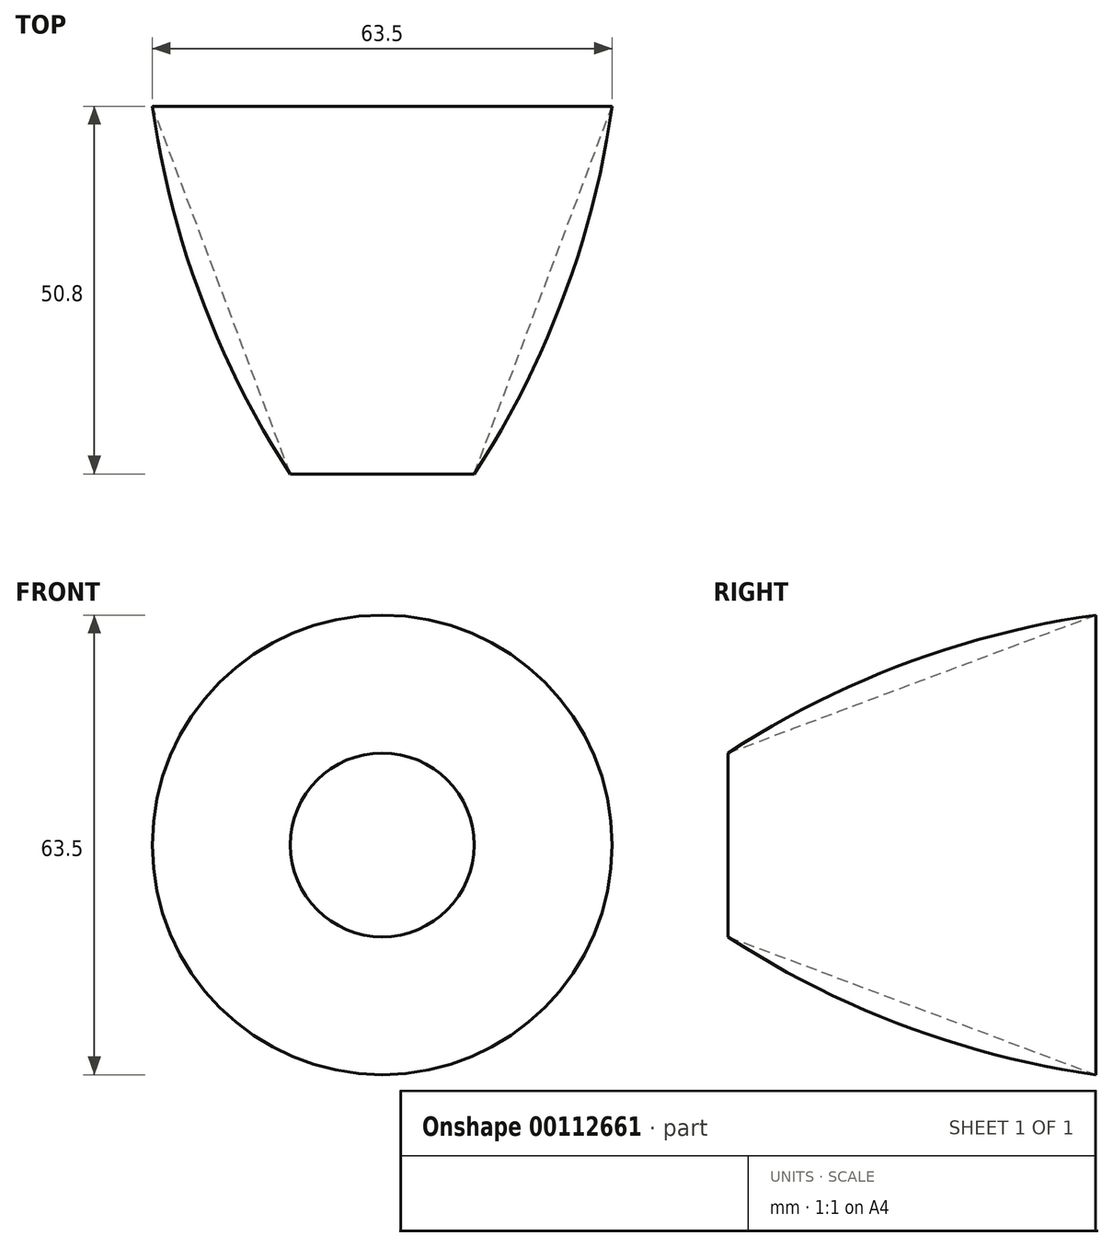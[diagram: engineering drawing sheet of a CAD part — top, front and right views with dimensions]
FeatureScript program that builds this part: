
annotation { "Feature Type Name" : "Feature", "Feature Type Description" : "" }
export const myFeature = defineFeature(function(context is Context, id is Id, definition is map)
    precondition{}
    {
        {
            var Q0;
            Q0=qCreatedBy(makeId("Top.planeOp"),FACE);
            var sketch = newSketch(context, id + "F0", { "sketchPlane" : qUnion([Q0])});
            skLineSegment(sketch, "E0", {"start": v(0, 0) * mm, "end": v(12.7, 0) * mm});
            skLineSegment(sketch, "E1", {"start": v(12.7, 0) * mm, "end": v(12.7, 50.8) * mm, "construction": true});
            skLineSegment(sketch, "E2", {"start": v(12.7, 50.8) * mm, "end": v(31.75, 50.8) * mm, "construction": true});
            skArc(sketch, "E3", {"start": v(12.7, 0) * mm, "mid": v(25.01, 24.35) * mm, "end": v(31.75, 50.8) * mm});
            skLineSegment(sketch, "E4", {"start": v(12.7, 0) * mm, "end": v(31.75, 50.8) * mm});
            skLineSegment(sketch, "E5", {"start": v(12.7, 25.4) * mm, "end": v(25.4, 25.4) * mm, "construction": true});
            skSolve(sketch);
        }
        {
            var Q0;
            Q0=qCreatedBy(makeId("Front.planeOp"),FACE);
            var sketch = newSketch(context, id + "F1", { "sketchPlane" : qUnion([Q0])});
            skCircle(sketch, "E6", {"center": v(0, 0) * mm, "radius": 12.7 * mm});
            skSolve(sketch);
        }
        {
            var Q0;
            Q0=makeQuery(id+"F0.imprint","IMPRINT",FACE,{"disambiguationData":[TD([[makeQuery(id+"F0.imprint","IMPRINT",EDGE,{"derivedFrom":sQuery(id+"F0.wireOp",EDGE,"E3")}),1.0]])]});
            var Q1;
            Q1=sQuery(id+"F1.wireOp",EDGE,"E6");
            revolve(context, id + "F2", {"entities" : qUnion([Q0]), "axis" : qUnion([Q1]), "revolveType" : RevolveType.FULL});
        }
    });
